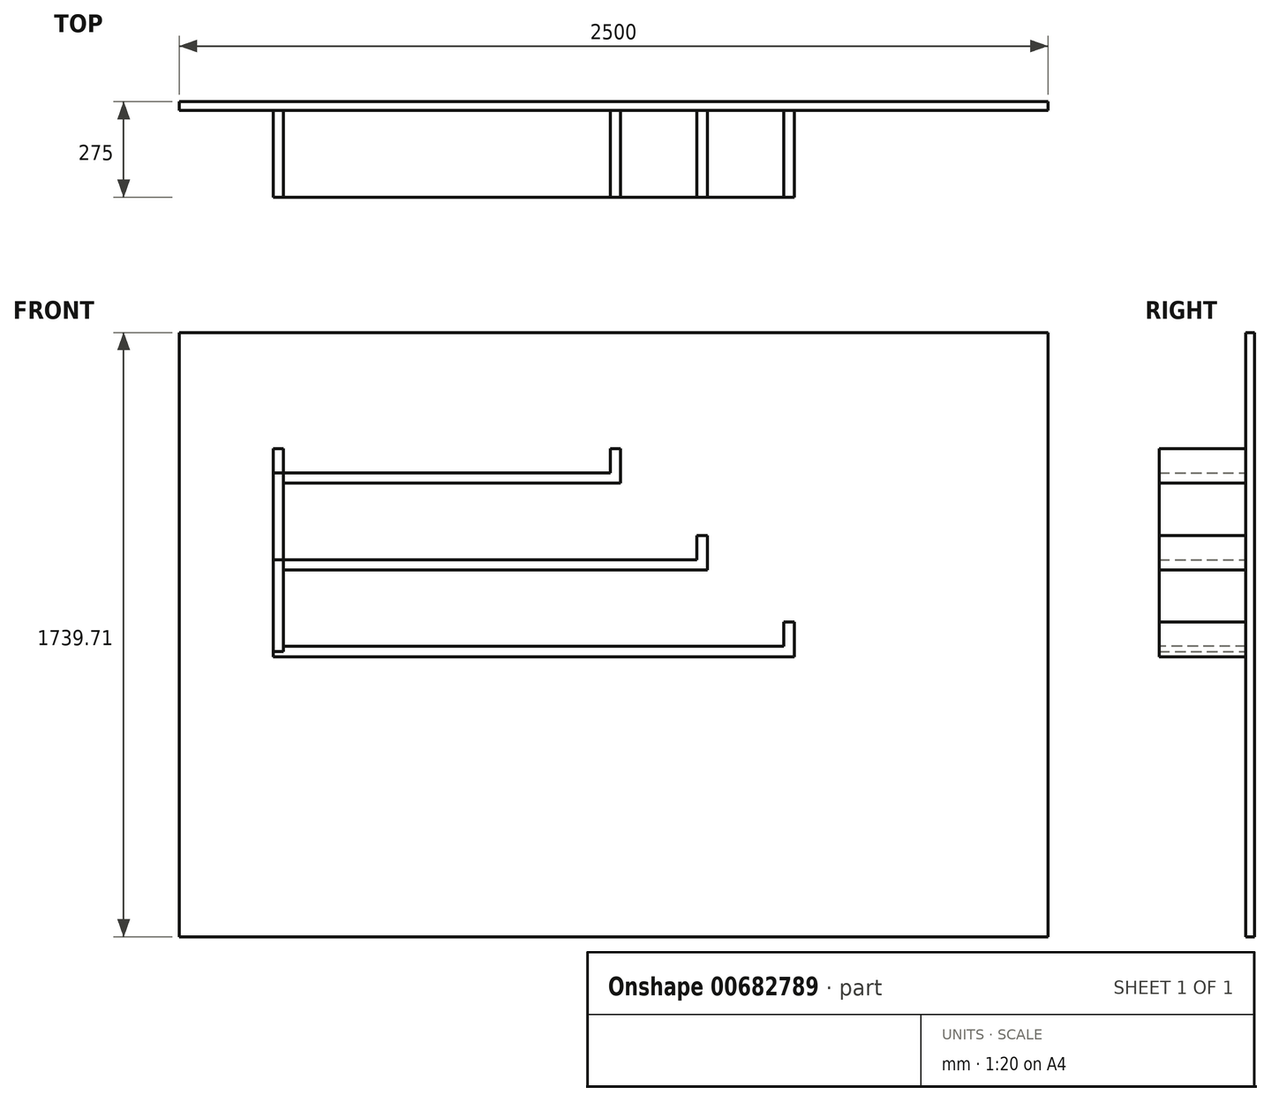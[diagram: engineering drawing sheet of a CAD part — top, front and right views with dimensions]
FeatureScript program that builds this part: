
annotation { "Feature Type Name" : "Feature", "Feature Type Description" : "" }
export const myFeature = defineFeature(function(context is Context, id is Id, definition is map)
    precondition{}
    {
        {
            var Q0;
            Q0=qCreatedBy(makeId("Front.planeOp"),FACE);
            var sketch = newSketch(context, id + "F0", { "sketchPlane" : qUnion([Q0])});
            skLineSegment(sketch, "E0.bottom", {"start": v(-284.96, 918.89) * mm, "end": v(2215.04, 918.89) * mm});
            skLineSegment(sketch, "E0.top", {"start": v(-284.96, -820.82) * mm, "end": v(2215.04, -820.82) * mm});
            skLineSegment(sketch, "E0.left", {"start": v(-284.96, 918.89) * mm, "end": v(-284.96, -820.82) * mm});
            skLineSegment(sketch, "E0.right", {"start": v(2215.04, 918.89) * mm, "end": v(2215.04, -820.82) * mm});
            skSolve(sketch);
        }
        {
            var Q0;
            Q0 = qSketchRegion(id + "F0", true);
            extrude(context, id + "F1", {"entities" : qUnion([Q0]), "oppositeDirection" : true, "depth" : 25 * mm, "offsetDistance" : 25 * mm});
        }
        {
            var Q0;
            Q0=qCreatedBy(makeId("Front.planeOp"),FACE);
            var sketch = newSketch(context, id + "F2", { "sketchPlane" : qUnion([Q0])});
            skLineSegment(sketch, "E1", {"start": v(0, 0) * mm, "end": v(0, 250) * mm});
            skLineSegment(sketch, "E2", {"start": v(0, 250) * mm, "end": v(1220, 250) * mm});
            skLineSegment(sketch, "E3", {"start": v(1220, 250) * mm, "end": v(1220, 335) * mm});
            skLineSegment(sketch, "E4", {"start": v(0, 250) * mm, "end": v(0, 500) * mm});
            skLineSegment(sketch, "E5", {"start": v(0, 500) * mm, "end": v(970, 500) * mm});
            skLineSegment(sketch, "E6", {"start": v(970, 500) * mm, "end": v(970, 585) * mm});
            skLineSegment(sketch, "E7", {"start": v(0, 0) * mm, "end": v(1470, 0) * mm});
            skLineSegment(sketch, "E8", {"start": v(1470, 0) * mm, "end": v(1470, 85) * mm});
            skLineSegment(sketch, "E9", {"start": v(0, 500) * mm, "end": v(0, 585) * mm});
            skSolve(sketch);
        }
        {
            var Q0;
            Q0=qCreatedBy(makeId("Top.planeOp"),FACE);
            var sketch = newSketch(context, id + "F3", { "sketchPlane" : qUnion([Q0])});
            skLineSegment(sketch, "E10.bottom", {"start": v(-15, -250) * mm, "end": v(15, -250) * mm});
            skLineSegment(sketch, "E10.top", {"start": v(-15, 0) * mm, "end": v(15, 0) * mm});
            skLineSegment(sketch, "E10.left", {"start": v(-15, -250) * mm, "end": v(-15, 0) * mm});
            skLineSegment(sketch, "E10.right", {"start": v(15, -250) * mm, "end": v(15, 0) * mm});
            skPoint(sketch, "E10.middle", {"position": v(0, -125) * mm});
            skSolve(sketch);
        }
        {
            var Q0;
            Q0 = qSketchRegion(id + "F3", true);
            var Q1;
            Q1=sQuery(id+"F2.wireOp",EDGE,"E1");
            var Q2;
            Q2=sQuery(id+"F2.wireOp",EDGE,"E4");
            var Q3;
            Q3=sQuery(id+"F2.wireOp",EDGE,"E9");
            var Q4;
            Q4=sQuery(id+"F2.wireOp",EDGE,"E7");
            var Q5;
            Q5=sQuery(id+"F2.wireOp",EDGE,"E8");
            sweep(context, id + "F4", {"profiles" : qUnion([Q0]), "path" : qUnion([Q1, Q2, Q3, Q4, Q5])});
        }
        {
            var Q0;
            Q0 = qSketchRegion(id + "F3", true);
            var Q1;
            Q1=sQuery(id+"F2.wireOp",EDGE,"E1");
            var Q2;
            Q2=sQuery(id+"F2.wireOp",EDGE,"E2");
            var Q3;
            Q3=sQuery(id+"F2.wireOp",EDGE,"E3");
            sweep(context, id + "F5", {"profiles" : qUnion([Q0]), "path" : qUnion([Q1, Q2, Q3])});
        }
        {
            var Q0;
            Q0 = qSketchRegion(id + "F3", true);
            var Q1;
            Q1=sQuery(id+"F2.wireOp",EDGE,"E1");
            var Q2;
            Q2=sQuery(id+"F2.wireOp",EDGE,"E4");
            var Q3;
            Q3=sQuery(id+"F2.wireOp",EDGE,"E5");
            var Q4;
            Q4=sQuery(id+"F2.wireOp",EDGE,"E6");
            sweep(context, id + "F6", {"profiles" : qUnion([Q0]), "path" : qUnion([Q1, Q2, Q3, Q4])});
        }
    });
